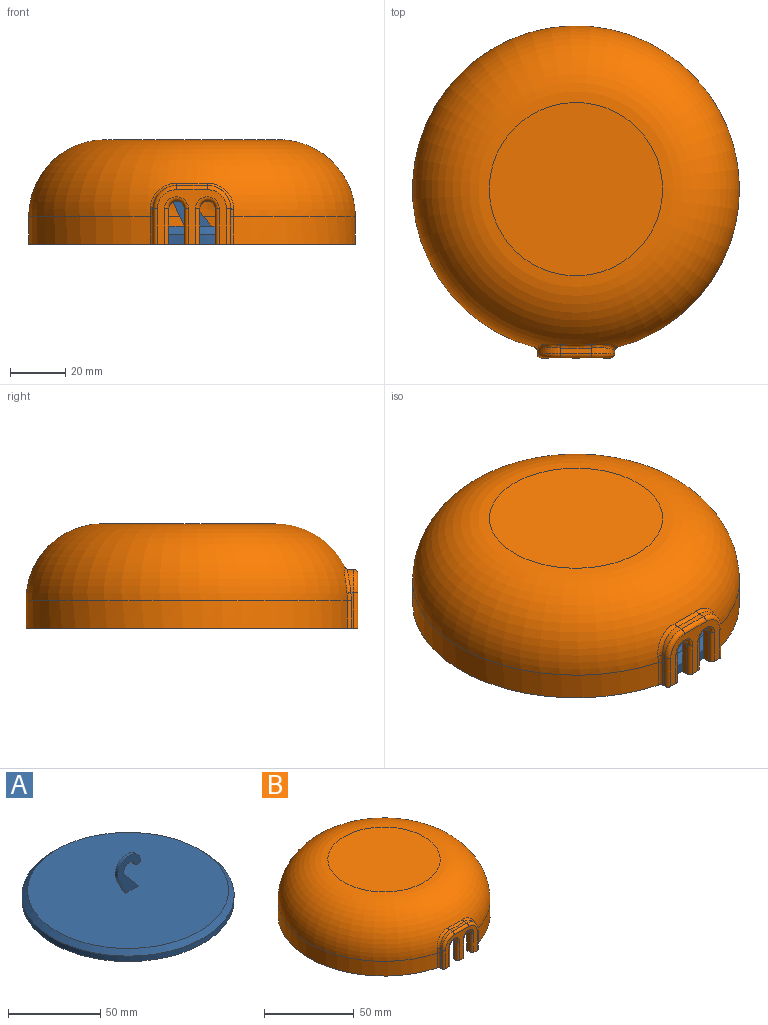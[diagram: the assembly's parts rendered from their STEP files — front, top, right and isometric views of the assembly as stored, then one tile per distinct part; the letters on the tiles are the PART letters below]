
ASSEMBLY  parts=2 mates=1
PART A: 11 faces, bbox 115x115x30.3 mm
  f0: plane 23.7x17.43mm, normal (0,1,0), area 197.4mm2, adj f2,f6,f7,f8,f9,f10
  f1: cylinder r=57.5mm len=115mm, axis (0,0,-1), area 1300.6mm2, adj f3,f4
  f2: plane 109x109mm, normal (0,0,1), area 9311.6mm2, adj f0,f4,f5,f9,f10
  f3: plane 115x115mm, normal (0,0,-1), area 10386.9mm2, adj f1
  f4: cone r=54.5mm half-angle=45deg, axis (0,0,-1), area 1492.8mm2, adj f1,f2
  f5: plane 23.7x17.43mm, normal (0,-1,0), area 197.4mm2, adj f2,f6,f7,f8,f9,f10
  f6: cylinder r=8.9mm len=17.3mm, axis (0,-1,0), area 57.8mm2, adj f0,f5,f7,f10
  f7: cylinder r=2.3mm len=4.47mm, axis (0,-1,0), area 14.5mm2, adj f0,f5,f6,f8
  f8: cylinder r=4.3mm len=8.36mm, axis (0,-1,0), area 30.2mm2, adj f0,f5,f7,f9
  f9: plane 12x10.31mm, normal (0.76,0,0.65), area 31.6mm2, adj f0,f2,f5,f8
  f10: plane 10.96x5.24mm, normal (-0.9,0,-0.43), area 24.3mm2, adj f0,f2,f5,f6
PART B: 56 faces, bbox 128x128x37.8 mm
  f0: plane 120.1x118.2mm, normal (0,0,-1), area 576.8mm2, adj f1,f5,f11,f12,f13,f14,f20,f22
  f1: cylinder r=57.5mm len=10.04mm, axis (0,0,-1), area 16.3mm2, adj f0,f4,f14,f31
  f2: cylinder r=57.5mm len=10.04mm, axis (0,0,-1), area 16.1mm2, adj f3,f7,f10,f27
  f3: torus R=31.34mm, axis (0,0,1), area 27.6mm2, adj f2,f10,f11,f16,f22,f27,f28,f33
  f4: torus R=31.34mm, axis (0,0,1), area 27.6mm2, adj f1,f9,f14,f15,f21,f26,f31,f32
  f5: cylinder r=59.1mm len=118.2mm, axis (0,0,-1), area 3420.1mm2, adj f0,f8,f38,f44
  f6: plane 62.67x62.67mm, normal (0,0,1), area 3085mm2, adj f8
  f7: plane 5.6x3.57mm, normal (0,0,-1), area 14.2mm2, adj f2,f9,f10,f20,f21,f26,f27,f37
  f8: torus R=31.34mm, axis (0,0,1), area 13091.4mm2, adj f5,f6,f39,f40,f41,f42,f43
  f9: plane 12.84x2.22mm, normal (-1,0,0), area 26.7mm2, adj f4,f7,f15,f21,f55
  f10: plane 12.84x2.22mm, normal (1,0,0), area 26.7mm2, adj f2,f3,f7,f16,f52
  f11: plane 12.85x2.78mm, normal (-1,0,0), area 33.7mm2, adj f0,f3,f16,f22,f50
  f12: plane 12.84x1.06mm, normal (1,0,0), area 11.9mm2, adj f0,f17,f43,f44,f45
  f13: plane 12.84x1.06mm, normal (-1,0,0), area 11.9mm2, adj f0,f19,f38,f39,f49
  f14: plane 12.85x2.78mm, normal (1,0,0), area 33.7mm2, adj f0,f1,f4,f15,f53
  f15: cylinder r=2.8mm len=5.6mm, axis (0,1,0), area 24mm2, adj f4,f9,f14,f54
  f16: cylinder r=2.8mm len=5.6mm, axis (0,1,0), area 24mm2, adj f3,f10,f11,f51
  f17: cylinder r=8.4mm len=8.4mm, axis (0,1,0), area 24mm2, adj f12,f18,f42,f46
  f18: plane 11.2x2.07mm, normal (0,0,1), area 21.2mm2, adj f17,f19,f41,f47
  f19: cylinder r=8.4mm len=8.4mm, axis (0,1,0), area 24mm2, adj f13,f18,f40,f48
  f20: plane 25x19.74mm, normal (0,-1,0), area 194.1mm2, adj f0,f7,f45,f46,f47,f48,f49,f50
  f21: cylinder r=57.5mm len=10.04mm, axis (0,0,-1), area 16.1mm2, adj f4,f7,f9,f26
  f22: cylinder r=57.5mm len=10.04mm, axis (0,0,-1), area 16.3mm2, adj f0,f3,f11,f28
  f23: cylinder r=57.5mm len=115mm, axis (0,0,-1), area 3375.2mm2, adj f0,f25,f29,f30
  f24: plane 62.67x62.67mm, normal (0,0,-1), area 3085mm2, adj f25
  f25: torus R=31.34mm, axis (0,0,1), area 12168.4mm2, adj f23,f24,f29,f30,f34,f35,f36
  f26: plane 12.84x2.06mm, normal (1,0,0), area 24.7mm2, adj f4,f7,f21,f32,f37
  f27: plane 12.84x2.06mm, normal (-1,0,0), area 24.7mm2, adj f2,f3,f7,f33,f37
  f28: plane 12.85x2.94mm, normal (1,0,0), area 35.8mm2, adj f0,f3,f22,f33,f37
  f29: plane 12.85x3.42mm, normal (-1,0,0), area 41.9mm2, adj f0,f23,f25,f34,f37
  f30: plane 12.85x3.42mm, normal (1,0,0), area 41.9mm2, adj f0,f23,f25,f36,f37
  f31: plane 12.85x2.94mm, normal (-1,0,0), area 35.8mm2, adj f0,f1,f4,f32,f37
  f32: cylinder r=4.4mm len=8.8mm, axis (0,1,0), area 40.2mm2, adj f4,f26,f31,f37
  f33: cylinder r=4.4mm len=8.8mm, axis (0,1,0), area 40.2mm2, adj f3,f27,f28,f37
  f34: cylinder r=6.8mm len=6.8mm, axis (0,1,0), area 41.7mm2, adj f25,f29,f35,f37
  f35: plane 11.2x4.01mm, normal (0,0,-1), area 42.8mm2, adj f25,f34,f36,f37
  f36: cylinder r=6.8mm len=6.8mm, axis (0,1,0), area 41.7mm2, adj f25,f30,f35,f37
  f37: plane 24.8x19.64mm, normal (0,1,0), area 180.4mm2, adj f0,f7,f26,f27,f28,f29,f30,f31
  f38: cylinder r=1.5mm len=10.04mm, axis (0,0,-1), area 19.8mm2, adj f0,f5,f13,f39
  f39: bspline ~8.53x1.98mm, area 5.4mm2, adj f8,f13,f38,f40
  f40: bspline ~11.79x11.48mm, area 24.9mm2, adj f8,f19,f39,f41
  f41: torus R=57.7mm, axis (0,0,1), area 18.6mm2, adj f8,f18,f40,f42
  f42: bspline ~11.79x11.48mm, area 24.9mm2, adj f8,f17,f41,f43
  f43: bspline ~8.53x1.98mm, area 5.4mm2, adj f8,f12,f42,f44
  f44: cylinder r=1.5mm len=10.04mm, axis (0,0,-1), area 19.8mm2, adj f0,f5,f12,f43
  f45: cylinder r=1.5mm len=12.84mm, axis (0,0,-1), area 30.2mm2, adj f0,f12,f20,f46
  f46: torus R=6.9mm, axis (0,-1,0), area 29.1mm2, adj f17,f20,f45,f47
  f47: cylinder r=1.5mm len=11.2mm, axis (1,0,0), area 26.4mm2, adj f18,f20,f46,f48
  f48: torus R=6.9mm, axis (0,-1,0), area 29.1mm2, adj f19,f20,f47,f49
  f49: cylinder r=1.5mm len=12.84mm, axis (0,0,1), area 30.2mm2, adj f0,f13,f20,f48
  f50: cylinder r=1.5mm len=12.84mm, axis (0,0,1), area 30.2mm2, adj f0,f11,f20,f51
  f51: torus R=4.3mm, axis (0,-1,0), area 24.8mm2, adj f16,f20,f50,f52
  f52: cylinder r=1.5mm len=12.84mm, axis (0,0,-1), area 30.2mm2, adj f7,f10,f20,f51
  f53: cylinder r=1.5mm len=12.84mm, axis (0,0,-1), area 30.2mm2, adj f0,f14,f20,f54
  f54: torus R=4.3mm, axis (0,-1,0), area 24.8mm2, adj f15,f20,f53,f55
  f55: cylinder r=1.5mm len=12.84mm, axis (0,0,1), area 30.2mm2, adj f7,f9,f20,f54
PLACE A t=(-5.13,-8.73,0)mm
PLACE B t=(-5.13,-8.73,0)mm
MATE revolute A.f1 <-> B.f1  axis (0,0,-1) through (-5.13,-8.73,0)mm
